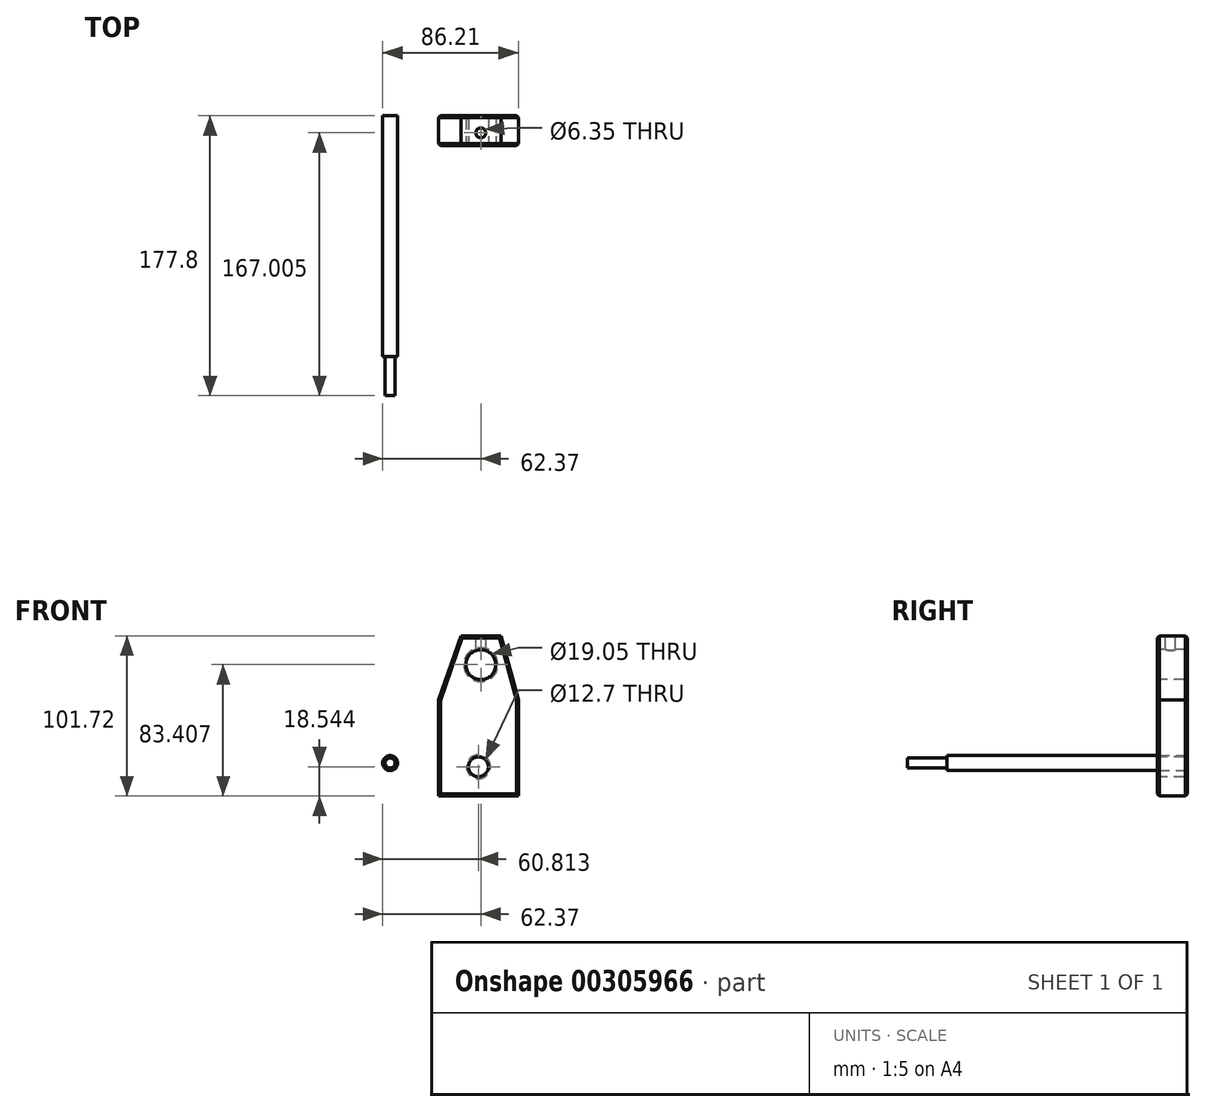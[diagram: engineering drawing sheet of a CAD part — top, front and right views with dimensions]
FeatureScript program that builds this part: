
annotation { "Feature Type Name" : "Feature", "Feature Type Description" : "" }
export const myFeature = defineFeature(function(context is Context, id is Id, definition is map)
    precondition{}
    {
        {
            var Q0;
            Q0=qCreatedBy(makeId("Front.planeOp"),FACE);
            var sketch = newSketch(context, id + "F0", { "sketchPlane" : qUnion([Q0])});
            skLineSegment(sketch, "E0", {"start": v(-21.05, -55.56) * mm, "end": v(-21.05, 5.4) * mm});
            skLineSegment(sketch, "E1", {"start": v(-21.05, -55.56) * mm, "end": v(29.75, -55.56) * mm});
            skLineSegment(sketch, "E2", {"start": v(29.75, -55.56) * mm, "end": v(29.75, 5.4) * mm});
            skLineSegment(sketch, "E3", {"start": v(29.75, 5.4) * mm, "end": v(-21.05, 5.4) * mm});
            skLineSegment(sketch, "E4", {"start": v(-21.05, 5.4) * mm, "end": v(-6.8, 46.16) * mm});
            skLineSegment(sketch, "E5", {"start": v(-6.8, 46.16) * mm, "end": v(18.6, 46.16) * mm});
            skLineSegment(sketch, "E6", {"start": v(18.6, 46.16) * mm, "end": v(29.75, 5.4) * mm});
            skSolve(sketch);
        }
        {
            var Q0;
            Q0=makeQuery(id+"F0.imprint","IMPRINT",FACE,{"disambiguationData":[TD([[makeQuery(id+"F0.imprint","IMPRINT",EDGE,{"derivedFrom":sQuery(id+"F0.wireOp",EDGE,"E3")}),-1.0]])]});
            var Q1;
            Q1=makeQuery(id+"F0.imprint","IMPRINT",FACE,{"disambiguationData":[TD([[makeQuery(id+"F0.imprint","IMPRINT",EDGE,{"derivedFrom":sQuery(id+"F0.wireOp",EDGE,"E0")}),-1.0]])]});
            extrude(context, id + "F1", {"entities" : qUnion([Q0, Q1]), "depth" : 19 * mm});
        }
        {
            var Q0;
            Q0=makeQuery(id+"F1.opExtrude","CAP_FACE",FACE,{"disambiguationData":[OSD([sQuery(id+"F0.wireOp",EDGE,"E0"),sQuery(id+"F0.wireOp",EDGE,"E1"),sQuery(id+"F0.wireOp",EDGE,"E2"),sQuery(id+"F0.wireOp",EDGE,"E4"),sQuery(id+"F0.wireOp",EDGE,"E5"),sQuery(id+"F0.wireOp",EDGE,"E6")])],"isStart":false});
            var sketch = newSketch(context, id + "F2", { "sketchPlane" : qUnion([Q0])});
            skLineSegment(sketch, "E7", {"start": v(5.9, 46.16) * mm, "end": v(5.9, 27.85) * mm});
            skCircle(sketch, "E8", {"center": v(5.9, 27.85) * mm, "radius": 9.53 * mm});
            skSolve(sketch);
        }
        {
            var Q0;
            Q0=makeQuery(id+"F2.imprint","IMPRINT",FACE,{"disambiguationData":[TD([[makeQuery(id+"F2.imprint","IMPRINT",EDGE,{"derivedFrom":sQuery(id+"F2.wireOp",EDGE,"E8")}),1.0]])]});
            extrude(context, id + "F3", {"entities" : qUnion([Q0]), "operationType" : NewBodyOperationType.REMOVE, "oppositeDirection" : true, "depth" : 25.4 * mm});
        }
        {
            var Q0;
            Q0=makeQuery(id+"F1.opExtrude","CAP_FACE",FACE,{"disambiguationData":[OSD([sQuery(id+"F0.wireOp",EDGE,"E0"),sQuery(id+"F0.wireOp",EDGE,"E1"),sQuery(id+"F0.wireOp",EDGE,"E2"),sQuery(id+"F0.wireOp",EDGE,"E4"),sQuery(id+"F0.wireOp",EDGE,"E5"),sQuery(id+"F0.wireOp",EDGE,"E6")])],"isStart":false});
            var sketch = newSketch(context, id + "F4", { "sketchPlane" : qUnion([Q0])});
            skLineSegment(sketch, "E9", {"start": v(4.35, -55.56) * mm, "end": v(4.35, -37.02) * mm});
            skCircle(sketch, "E10", {"center": v(4.35, -37.02) * mm, "radius": 6.35 * mm});
            skSolve(sketch);
        }
        {
            var Q0;
            Q0=makeQuery(id+"F4.imprint","IMPRINT",FACE,{"disambiguationData":[TD([[makeQuery(id+"F4.imprint","IMPRINT",EDGE,{"derivedFrom":sQuery(id+"F4.wireOp",EDGE,"E10")}),1.0]])]});
            extrude(context, id + "F5", {"entities" : qUnion([Q0]), "operationType" : NewBodyOperationType.REMOVE, "oppositeDirection" : true, "depth" : 25.4 * mm});
        }
        {
            var Q0;
            Q0=makeQuery(id+"F1.opExtrude","CAP_EDGE",EDGE,{"disambiguationData":[OSD([sQuery(id+"F0.wireOp",EDGE,"E6")])],"isStart":false});
            var Q1;
            Q1=makeQuery(id+"F1.opExtrude","CAP_EDGE",EDGE,{"disambiguationData":[OSD([sQuery(id+"F0.wireOp",EDGE,"E5")])],"isStart":false});
            var Q2;
            Q2=makeQuery(id+"F1.opExtrude","CAP_EDGE",EDGE,{"disambiguationData":[OSD([sQuery(id+"F0.wireOp",EDGE,"E4")])],"isStart":false});
            var Q3;
            Q3=makeQuery(id+"F1.opExtrude","CAP_EDGE",EDGE,{"disambiguationData":[OSD([sQuery(id+"F0.wireOp",EDGE,"E0")])],"isStart":false});
            var Q4;
            Q4=makeQuery(id+"F1.opExtrude","CAP_EDGE",EDGE,{"disambiguationData":[OSD([sQuery(id+"F0.wireOp",EDGE,"E1")])],"isStart":false});
            var Q5;
            Q5=makeQuery(id+"F1.opExtrude","CAP_EDGE",EDGE,{"disambiguationData":[OSD([sQuery(id+"F0.wireOp",EDGE,"E2")])],"isStart":false});
            var Q6;
            Q6=makeQuery(id+"F5.boolean.opBoolean","COPY",EDGE,{"derivedFrom":makeQuery(id+"F5.opExtrude","CAP_EDGE",EDGE,{"disambiguationData":[OSD([sQuery(id+"F4.wireOp",EDGE,"E10")])],"isStart":true})});
            var Q7;
            Q7=makeQuery(id+"F3.boolean.opBoolean","COPY",EDGE,{"derivedFrom":makeQuery(id+"F3.opExtrude","CAP_EDGE",EDGE,{"disambiguationData":[OSD([sQuery(id+"F2.wireOp",EDGE,"E8")])],"isStart":true})});
            chamfer(context, id + "F6", {"entities" : qUnion([Q0, Q1, Q2, Q3, Q4, Q5, Q6, Q7]), "width" : 1.27 * mm, "tangentPropagation" : true});
        }
        {
            var Q0;
            Q0=makeQuery(id+"F1.opExtrude","CAP_EDGE",EDGE,{"disambiguationData":[OSD([sQuery(id+"F0.wireOp",EDGE,"E5")])],"isStart":true});
            var Q1;
            Q1=makeQuery(id+"F1.opExtrude","CAP_EDGE",EDGE,{"disambiguationData":[OSD([sQuery(id+"F0.wireOp",EDGE,"E4")])],"isStart":true});
            var Q2;
            Q2=makeQuery(id+"F1.opExtrude","CAP_EDGE",EDGE,{"disambiguationData":[OSD([sQuery(id+"F0.wireOp",EDGE,"E0")])],"isStart":true});
            var Q3;
            Q3=makeQuery(id+"F1.opExtrude","CAP_EDGE",EDGE,{"disambiguationData":[OSD([sQuery(id+"F0.wireOp",EDGE,"E1")])],"isStart":true});
            var Q4;
            Q4=makeQuery(id+"F1.opExtrude","CAP_EDGE",EDGE,{"disambiguationData":[OSD([sQuery(id+"F0.wireOp",EDGE,"E2")])],"isStart":true});
            var Q5;
            Q5=makeQuery(id+"F1.opExtrude","CAP_EDGE",EDGE,{"disambiguationData":[OSD([sQuery(id+"F0.wireOp",EDGE,"E6")])],"isStart":true});
            var Q6;
            Q6=makeQuery(id+"F3.boolean.opBoolean","INTERSECT",EDGE,{"derivedFrom":[makeQuery(id+"F1.opExtrude","CAP_FACE",FACE,{"disambiguationData":[OSD([sQuery(id+"F0.wireOp",EDGE,"E0"),sQuery(id+"F0.wireOp",EDGE,"E1"),sQuery(id+"F0.wireOp",EDGE,"E2"),sQuery(id+"F0.wireOp",EDGE,"E4"),sQuery(id+"F0.wireOp",EDGE,"E5"),sQuery(id+"F0.wireOp",EDGE,"E6")])],"isStart":true}),makeQuery(id+"F3.opExtrude","SWEPT_FACE",FACE,{"disambiguationData":[OSD([sQuery(id+"F2.wireOp",EDGE,"E8")])]})]});
            var Q7;
            Q7=makeQuery(id+"F5.boolean.opBoolean","INTERSECT",EDGE,{"derivedFrom":[makeQuery(id+"F1.opExtrude","CAP_FACE",FACE,{"disambiguationData":[OSD([sQuery(id+"F0.wireOp",EDGE,"E0"),sQuery(id+"F0.wireOp",EDGE,"E1"),sQuery(id+"F0.wireOp",EDGE,"E2"),sQuery(id+"F0.wireOp",EDGE,"E4"),sQuery(id+"F0.wireOp",EDGE,"E5"),sQuery(id+"F0.wireOp",EDGE,"E6")])],"isStart":true}),makeQuery(id+"F5.opExtrude","SWEPT_FACE",FACE,{"disambiguationData":[OSD([sQuery(id+"F4.wireOp",EDGE,"E10")])]})]});
            chamfer(context, id + "F7", {"entities" : qUnion([Q0, Q1, Q2, Q3, Q4, Q5, Q6, Q7]), "width" : 1.27 * mm, "tangentPropagation" : true});
        }
        {
            var Q0;
            Q0=makeQuery(id+"F1.opExtrude","SWEPT_FACE",FACE,{"disambiguationData":[OSD([sQuery(id+"F0.wireOp",EDGE,"E5")])]});
            var sketch = newSketch(context, id + "F8", { "sketchPlane" : qUnion([Q0])});
            skLineSegment(sketch, "E11", {"start": v(5.9, -1.27) * mm, "end": v(5.9, -10.8) * mm});
            skCircle(sketch, "E12", {"center": v(5.9, -10.8) * mm, "radius": 3.18 * mm});
            skSolve(sketch);
        }
        {
            var Q0;
            Q0=makeQuery(id+"F8.imprint","IMPRINT",FACE,{"disambiguationData":[TD([[makeQuery(id+"F8.imprint","IMPRINT",EDGE,{"derivedFrom":sQuery(id+"F8.wireOp",EDGE,"E12")}),1.0]])]});
            extrude(context, id + "F9", {"entities" : qUnion([Q0]), "operationType" : NewBodyOperationType.REMOVE, "oppositeDirection" : true, "depth" : 25.4 * mm});
        }
        {
            var Q0;
            Q0=qCreatedBy(makeId("Front.planeOp"),FACE);
            var sketch = newSketch(context, id + "F10", { "sketchPlane" : qUnion([Q0])});
            skCircle(sketch, "E13", {"center": v(-51.7, -34.64) * mm, "radius": 4.76 * mm});
            skSolve(sketch);
        }
        {
            var Q0;
            Q0=makeQuery(id+"F10.imprint","IMPRINT",FACE,{"disambiguationData":[TD([[makeQuery(id+"F10.imprint","IMPRINT",EDGE,{"derivedFrom":sQuery(id+"F10.wireOp",EDGE,"E13")}),1.0]])]});
            extrude(context, id + "F11", {"entities" : qUnion([Q0]), "depth" : 152.9 * mm});
        }
        {
            var Q0;
            Q0=makeQuery(id+"F11.opExtrude","CAP_FACE",FACE,{"disambiguationData":[OSD([sQuery(id+"F10.wireOp",EDGE,"E13")])],"isStart":false});
            var sketch = newSketch(context, id + "F12", { "sketchPlane" : qUnion([Q0])});
            skCircle(sketch, "E14", {"center": v(-51.7, -34.64) * mm, "radius": 3.18 * mm});
            skSolve(sketch);
        }
        {
            var Q0;
            Q0=makeQuery(id+"F12.imprint","IMPRINT",FACE,{"disambiguationData":[TD([[makeQuery(id+"F12.imprint","IMPRINT",EDGE,{"derivedFrom":sQuery(id+"F12.wireOp",EDGE,"E14")}),1.0]])]});
            extrude(context, id + "F13", {"entities" : qUnion([Q0]), "operationType" : NewBodyOperationType.ADD, "depth" : 24.9 * mm});
        }
    });
